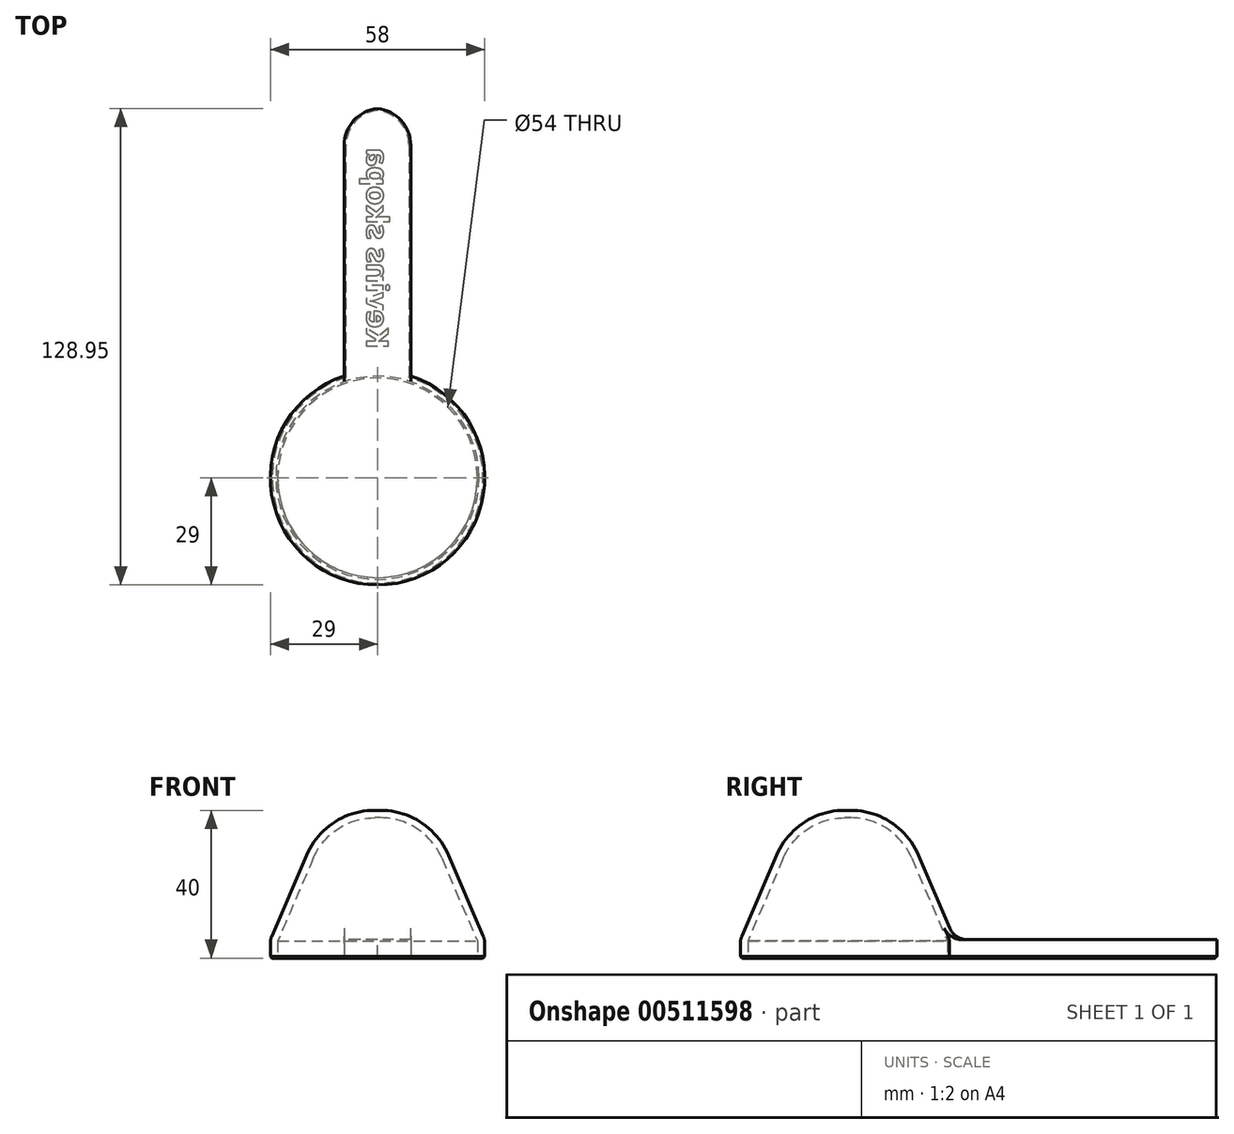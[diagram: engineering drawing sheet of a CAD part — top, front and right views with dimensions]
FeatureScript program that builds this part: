
annotation { "Feature Type Name" : "Feature", "Feature Type Description" : "" }
export const myFeature = defineFeature(function(context is Context, id is Id, definition is map)
    precondition{}
    {
        {
            var Q0;
            Q0=qCreatedBy(makeId("Top.planeOp"),FACE);
            var sketch = newSketch(context, id + "F0", { "sketchPlane" : qUnion([Q0])});
            skCircle(sketch, "E0", {"center": v(0, 0) * mm, "radius": 27 * mm});
            skCircle(sketch, "E1", {"center": v(0, 0) * mm, "radius": 29 * mm});
            skLineSegment(sketch, "E2.top", {"start": v(-9, 100) * mm, "end": v(9, 100) * mm});
            skLineSegment(sketch, "E2.left", {"start": v(-9, 27.57) * mm, "end": v(-9, 100) * mm});
            skLineSegment(sketch, "E2.right", {"start": v(9, 27.57) * mm, "end": v(9, 100) * mm});
            skSolve(sketch);
        }
        {
            var Q0;
            Q0=makeQuery(id+"F0.imprint","IMPRINT",FACE,{"disambiguationData":[TD([[makeQuery(id+"F0.imprint","IMPRINT",EDGE,{"derivedFrom":sQuery(id+"F0.wireOp",EDGE,"E0")}),-1.0]])]});
            var Q1;
            Q1=makeQuery(id+"F0.imprint","IMPRINT",FACE,{"disambiguationData":[TD([[makeQuery(id+"F0.imprint","IMPRINT",EDGE,{"derivedFrom":sQuery(id+"F0.wireOp",EDGE,"E0")}),1.0]])]});
            extrude(context, id + "F1", {"entities" : qUnion([Q0, Q1]), "depth" : 40 * mm, "offsetDistance" : 25 * mm});
        }
        {
            var Q0;
            Q0=makeQuery(id+"F1.opExtrude","CAP_EDGE",EDGE,{"disambiguationData":[OSD([sQuery(id+"F0.wireOp",EDGE,"E1")])],"isStart":false});
            chamfer(context, id + "F2", {"entities" : qUnion([Q0]), "chamferType" : ChamferType.TWO_OFFSETS, "width1" : 15 * mm, "oppositeDirection" : false, "width2" : 35 * mm, "tangentPropagation" : true});
        }
        {
            var Q0;
            {var subQ0=sQuery(id+"F0.wireOp",EDGE,"E1");Q0=makeQuery(id+"F2.opChamfer","BLEND_EDGE",EDGE,{"blendedFrom":[makeQuery(id+"F1.opExtrude","CAP_EDGE",EDGE,{"disambiguationData":[OSD([subQ0])],"isStart":false}),makeQuery(id+"F1.opExtrude","CAP_FACE",FACE,{"disambiguationData":[OSD([subQ0])],"isStart":false})],"blendedInto":[makeQuery(id+"F1.opExtrude","CAP_FACE",FACE,{"disambiguationData":[OSD([subQ0])],"isStart":false})]});}
            fillet(context, id + "F3", {"entities" : qUnion([Q0]), "radius" : 20 * mm, "tangentPropagation" : true, "allowEdgeOverflow" : false});
        }
        {
            var Q0;
            Q0=makeQuery(id+"F1.opExtrude","CAP_FACE",FACE,{"disambiguationData":[OSD([sQuery(id+"F0.wireOp",EDGE,"E1")])],"isStart":true});
            shell(context, id + "F4", {"entities" : qUnion([Q0]), "thickness" : 2 * mm});
        }
        {
            var Q0;
            Q0=makeQuery(id+"F0.imprint","IMPRINT",FACE,{"disambiguationData":[TD([[makeQuery(id+"F0.imprint","IMPRINT",EDGE,{"derivedFrom":sQuery(id+"F0.wireOp",EDGE,"E2.top")}),-1.0]])]});
            extrude(context, id + "F5", {"entities" : qUnion([Q0]), "operationType" : NewBodyOperationType.ADD, "depth" : 5 * mm, "offsetDistance" : 25 * mm});
        }
        {
            var Q0;
            Q0=makeQuery(id+"F5.opExtrude","SWEPT_EDGE",EDGE,{"disambiguationData":[OSD([sQuery(id+"F0.wireOp",EDGE,"E2.top"),sQuery(id+"F0.wireOp",EDGE,"E2.right")])]});
            var Q1;
            Q1=makeQuery(id+"F5.opExtrude","SWEPT_EDGE",EDGE,{"disambiguationData":[OSD([sQuery(id+"F0.wireOp",EDGE,"E1"),sQuery(id+"F0.wireOp",EDGE,"E2.left")])]});
            var Q2;
            Q2=makeQuery(id+"F5.opExtrude","SWEPT_EDGE",EDGE,{"disambiguationData":[OSD([sQuery(id+"F0.wireOp",EDGE,"E1"),sQuery(id+"F0.wireOp",EDGE,"E2.right")])]});
            var Q3;
            Q3=makeQuery(id+"F5.opExtrude","SWEPT_EDGE",EDGE,{"disambiguationData":[OSD([sQuery(id+"F0.wireOp",EDGE,"E2.top"),sQuery(id+"F0.wireOp",EDGE,"E2.left")])]});
            fillet(context, id + "F6", {"entities" : qUnion([Q0, Q1, Q2, Q3]), "radius" : 10 * mm, "tangentPropagation" : true, "allowEdgeOverflow" : false});
        }
        {
            var Q0;
            {var subQ0=sQuery(id+"F0.wireOp",EDGE,"E1");Q0=makeQuery(id+"F5.boolean.opBoolean","MERGE",EDGE,{"derivedFrom":[makeQuery(id+"F2.opChamfer","BLEND_EDGE",EDGE,{"blendedFrom":[makeQuery(id+"F1.opExtrude","CAP_EDGE",EDGE,{"disambiguationData":[OSD([subQ0])],"isStart":false}),makeQuery(id+"F1.opExtrude","SWEPT_FACE",FACE,{"disambiguationData":[OSD([subQ0])]})],"blendedInto":[makeQuery(id+"F1.opExtrude","SWEPT_FACE",FACE,{"disambiguationData":[OSD([subQ0])]})]}),makeQuery(id+"F5.opExtrude","CAP_EDGE",EDGE,{"disambiguationData":[OSD([subQ0])],"isStart":false})]});}
            fillet(context, id + "F7", {"entities" : qUnion([Q0]), "radius" : 5 * mm, "tangentPropagation" : true, "allowEdgeOverflow" : false});
        }
        {
            var Q0;
            {var subQ0=sQuery(id+"F0.wireOp",EDGE,"E1");Q0=makeQuery(id+"F5.boolean.opBoolean","SPLIT",EDGE,{"derivedFrom":makeQuery(id+"F2.opChamfer","BLEND_EDGE",EDGE,{"blendedFrom":[makeQuery(id+"F1.opExtrude","CAP_EDGE",EDGE,{"disambiguationData":[OSD([subQ0])],"isStart":false}),makeQuery(id+"F1.opExtrude","SWEPT_FACE",FACE,{"disambiguationData":[OSD([subQ0])]})],"blendedInto":[makeQuery(id+"F1.opExtrude","SWEPT_FACE",FACE,{"disambiguationData":[OSD([subQ0])]})]})});}
            fillet(context, id + "F8", {"entities" : qUnion([Q0]), "radius" : 5 * mm, "tangentPropagation" : true, "allowEdgeOverflow" : false});
        }
        {
            var Q0;
            {var subQ0=sQuery(id+"F0.wireOp",EDGE,"E2.right");var subQ1=sQuery(id+"F0.wireOp",EDGE,"E2.left");var subQ2=sQuery(id+"F0.wireOp",EDGE,"E2.top");var subQ3=sQuery(id+"F0.wireOp",EDGE,"E1");var subQ6=makeQuery(id+"F1.opExtrude","SWEPT_FACE",FACE,{"disambiguationData":[OSD([subQ3])]});Q0=makeQuery(id+"F11.boolean.opBoolean","SPLIT",FACE,{"disambiguationData":[TD([subQ6])],"derivedFrom":makeQuery(id+"F5.boolean.opBoolean","MERGE",FACE,{"derivedFrom":[makeQuery(id+"F1.opExtrude","CAP_FACE",FACE,{"disambiguationData":[OSD([subQ3])],"isStart":true}),makeQuery(id+"F5.opExtrude","CAP_FACE",FACE,{"disambiguationData":[OSD([subQ3,subQ2,subQ1,subQ0])],"isStart":true})]})});}
            chamfer(context, id + "F9", {"entities" : qUnion([Q0]), "width" : 0.5 * mm, "tangentPropagation" : true});
        }
        {
            var Q0;
            {var subQ0=sQuery(id+"F0.wireOp",EDGE,"E1");Q0=makeQuery(id+"F5.boolean.opBoolean","MERGE",FACE,{"derivedFrom":[makeQuery(id+"F1.opExtrude","CAP_FACE",FACE,{"disambiguationData":[OSD([subQ0])],"isStart":true}),makeQuery(id+"F5.opExtrude","CAP_FACE",FACE,{"disambiguationData":[OSD([subQ0,sQuery(id+"F0.wireOp",EDGE,"E2.top"),sQuery(id+"F0.wireOp",EDGE,"E2.left"),sQuery(id+"F0.wireOp",EDGE,"E2.right")])],"isStart":true})]});}
            var sketch = newSketch(context, id + "F10", { "sketchPlane" : qUnion([Q0])});
            skText(sketch, "E3", { "text": "Kevins skopa", "fontName": "OpenSans-Bold.ttf"});
            const initialGuessF10  = {"E3": [-0.003, -0.035, 0, -1, 0.006]};
            skSetInitialGuess(sketch, initialGuessF10);
            skSolve(sketch);
        }
        {
            var Q0;
            Q0 = qSketchRegion(id + "F10", true);
            extrude(context, id + "F11", {"entities" : qUnion([Q0]), "operationType" : NewBodyOperationType.REMOVE, "oppositeDirection" : true, "depth" : 0.1 * mm, "offsetDistance" : 25 * mm});
        }
    });
